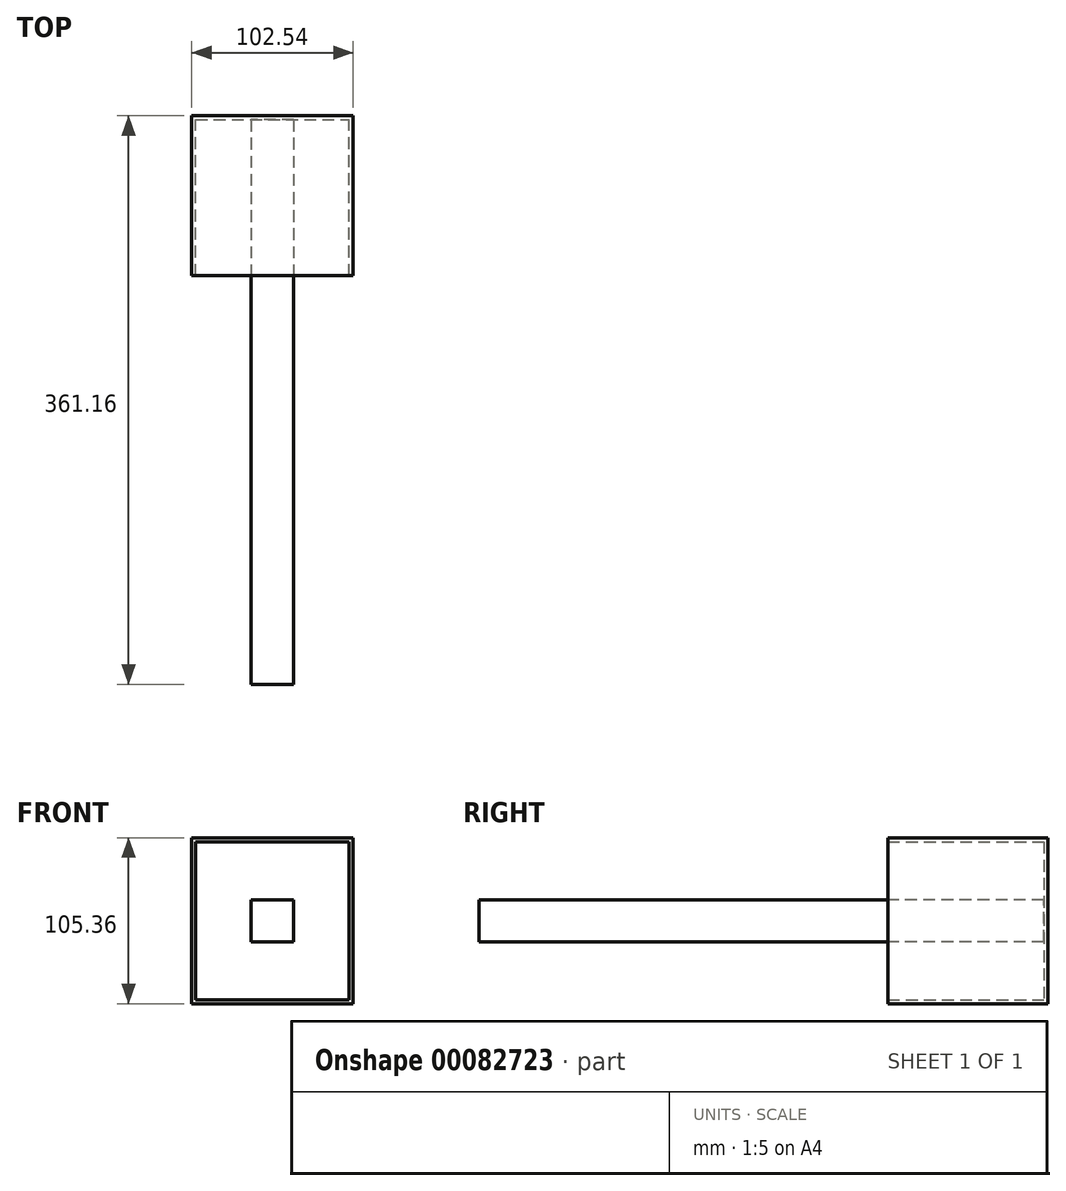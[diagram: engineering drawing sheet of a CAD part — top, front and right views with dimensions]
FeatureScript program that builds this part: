
annotation { "Feature Type Name" : "Feature", "Feature Type Description" : "" }
export const myFeature = defineFeature(function(context is Context, id is Id, definition is map)
    precondition{}
    {
        {
            var Q0;
            Q0=qCreatedBy(makeId("Front.planeOp"),FACE);
            var sketch = newSketch(context, id + "F0", { "sketchPlane" : qUnion([Q0])});
            skLineSegment(sketch, "E0.bottom", {"start": v(-51.27, 52.68) * mm, "end": v(51.27, 52.68) * mm});
            skLineSegment(sketch, "E0.top", {"start": v(-51.27, -52.68) * mm, "end": v(51.27, -52.68) * mm});
            skLineSegment(sketch, "E0.left", {"start": v(-51.27, 52.68) * mm, "end": v(-51.27, -52.68) * mm});
            skLineSegment(sketch, "E0.right", {"start": v(51.27, 52.68) * mm, "end": v(51.27, -52.68) * mm});
            skPoint(sketch, "E0.middle", {"position": v(0, 0) * mm});
            skSolve(sketch);
        }
        {
            var Q0;
            Q0=makeQuery(id+"F0.imprint","IMPRINT",FACE,{"disambiguationData":[TD([[makeQuery(id+"F0.imprint","IMPRINT",EDGE,{"derivedFrom":sQuery(id+"F0.wireOp",EDGE,"E0.bottom")}),-1.0]])]});
            extrude(context, id + "F1", {"entities" : qUnion([Q0]), "endBound" : BoundingType.SYMMETRIC, "depth" : 101.6 * mm});
        }
        {
            var Q0;
            Q0=makeQuery(id+"F1.opExtrude","CAP_FACE",FACE,{"disambiguationData":[OSD([sQuery(id+"F0.wireOp",EDGE,"E0.bottom"),sQuery(id+"F0.wireOp",EDGE,"E0.top"),sQuery(id+"F0.wireOp",EDGE,"E0.left"),sQuery(id+"F0.wireOp",EDGE,"E0.right")])],"isStart":false});
            shell(context, id + "F2", {"entities" : qUnion([Q0]), "thickness" : 2.54 * mm});
        }
        {
            var Q0;
            Q0=qCreatedBy(makeId("Front.planeOp"),FACE);
            var sketch = newSketch(context, id + "F3", { "sketchPlane" : qUnion([Q0])});
            skLineSegment(sketch, "E1.bottom", {"start": v(-13.57, 13.29) * mm, "end": v(13.57, 13.29) * mm});
            skLineSegment(sketch, "E1.top", {"start": v(-13.57, -13.29) * mm, "end": v(13.57, -13.29) * mm});
            skLineSegment(sketch, "E1.left", {"start": v(-13.57, 13.29) * mm, "end": v(-13.57, -13.29) * mm});
            skLineSegment(sketch, "E1.right", {"start": v(13.57, 13.29) * mm, "end": v(13.57, -13.29) * mm});
            skPoint(sketch, "E1.middle", {"position": v(0, 0) * mm});
            skCircle(sketch, "E2.cCircle", {"center": v(0, 0) * mm, "radius": 86.16 * mm, "construction": true});
            skLineSegment(sketch, "E2.0", {"start": v(-75.06, 42.3) * mm, "end": v(-60.1, 61.74) * mm});
            skLineSegment(sketch, "E2.1", {"start": v(-60.1, 61.74) * mm, "end": v(-40.27, 76.17) * mm});
            skLineSegment(sketch, "E2.2", {"start": v(-40.27, 76.17) * mm, "end": v(-17.18, 84.43) * mm});
            skLineSegment(sketch, "E2.3", {"start": v(-17.18, 84.43) * mm, "end": v(7.3, 85.85) * mm});
            skLineSegment(sketch, "E2.4", {"start": v(7.3, 85.85) * mm, "end": v(31.2, 80.32) * mm});
            skLineSegment(sketch, "E2.5", {"start": v(31.2, 80.32) * mm, "end": v(52.56, 68.27) * mm});
            skLineSegment(sketch, "E2.6", {"start": v(52.56, 68.27) * mm, "end": v(69.67, 50.7) * mm});
            skLineSegment(sketch, "E2.7", {"start": v(69.67, 50.7) * mm, "end": v(81.13, 29.02) * mm});
            skLineSegment(sketch, "E2.8", {"start": v(81.13, 29.02) * mm, "end": v(86.02, 4.99) * mm});
            skLineSegment(sketch, "E2.9", {"start": v(86.02, 4.99) * mm, "end": v(83.94, -19.45) * mm});
            skLineSegment(sketch, "E2.10", {"start": v(83.94, -19.45) * mm, "end": v(75.06, -42.3) * mm});
            skLineSegment(sketch, "E2.11", {"start": v(75.06, -42.3) * mm, "end": v(60.1, -61.74) * mm});
            skLineSegment(sketch, "E2.12", {"start": v(60.1, -61.74) * mm, "end": v(40.27, -76.17) * mm});
            skLineSegment(sketch, "E2.13", {"start": v(40.27, -76.17) * mm, "end": v(17.18, -84.43) * mm});
            skLineSegment(sketch, "E2.14", {"start": v(17.18, -84.43) * mm, "end": v(-7.3, -85.85) * mm});
            skLineSegment(sketch, "E2.15", {"start": v(-7.3, -85.85) * mm, "end": v(-31.2, -80.32) * mm});
            skLineSegment(sketch, "E2.16", {"start": v(-31.2, -80.32) * mm, "end": v(-52.56, -68.27) * mm});
            skLineSegment(sketch, "E2.17", {"start": v(-52.56, -68.27) * mm, "end": v(-69.67, -50.7) * mm});
            skLineSegment(sketch, "E2.18", {"start": v(-69.67, -50.7) * mm, "end": v(-81.13, -29.02) * mm});
            skLineSegment(sketch, "E2.19", {"start": v(-81.13, -29.02) * mm, "end": v(-86.02, -4.99) * mm});
            skLineSegment(sketch, "E2.20", {"start": v(-86.02, -4.99) * mm, "end": v(-83.94, 19.45) * mm});
            skLineSegment(sketch, "E2.21", {"start": v(-83.94, 19.45) * mm, "end": v(-75.06, 42.3) * mm});
            skSolve(sketch);
        }
        {
            var Q0;
            Q0=makeQuery(id+"F3.imprint","IMPRINT",FACE,{"disambiguationData":[TD([[makeQuery(id+"F3.imprint","IMPRINT",EDGE,{"derivedFrom":sQuery(id+"F3.wireOp",EDGE,"E1.bottom")}),-1.0]])]});
            var Q1;
            Q1=makeQuery(id+"F2.opShell","OFFSET_FACE",FACE,{"disambiguationData":[OSD([sQuery(id+"F0.wireOp",EDGE,"E0.bottom"),sQuery(id+"F0.wireOp",EDGE,"E0.top"),sQuery(id+"F0.wireOp",EDGE,"E0.left"),sQuery(id+"F0.wireOp",EDGE,"E0.right")])]});
            extrude(context, id + "F4", {"entities" : qUnion([Q0]), "operationType" : NewBodyOperationType.ADD, "endBound" : BoundingType.UP_TO_SURFACE, "oppositeDirection" : true, "endBoundEntityFace" : qUnion([Q1]), "depth" : 25.4 * mm});
        }
        {
            var Q0;
            Q0=makeQuery(id+"F4.opExtrude","CAP_FACE",FACE,{"disambiguationData":[OSD([sQuery(id+"F3.wireOp",EDGE,"E1.bottom"),sQuery(id+"F3.wireOp",EDGE,"E1.top"),sQuery(id+"F3.wireOp",EDGE,"E1.left"),sQuery(id+"F3.wireOp",EDGE,"E1.right")])],"isStart":true});
            extrude(context, id + "F5", {"entities" : qUnion([Q0]), "operationType" : NewBodyOperationType.ADD, "depth" : 310.36 * mm});
        }
    });
